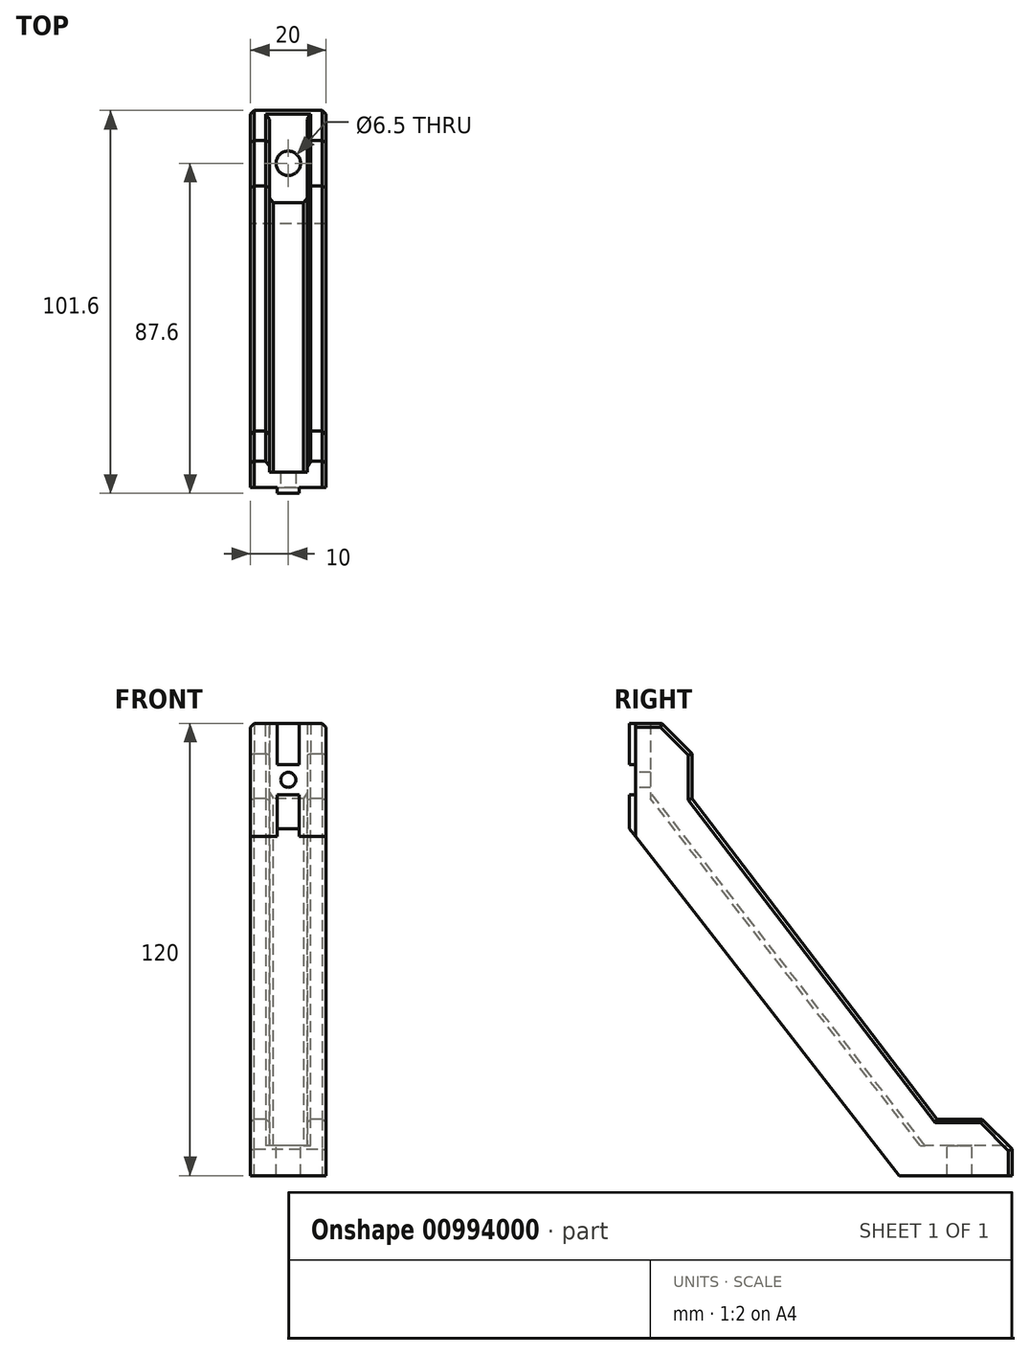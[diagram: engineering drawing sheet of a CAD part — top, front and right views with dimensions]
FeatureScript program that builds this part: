
annotation { "Feature Type Name" : "Feature", "Feature Type Description" : "" }
export const myFeature = defineFeature(function(context is Context, id is Id, definition is map)
    precondition{}
    {
        {
            var Q0;
            Q0=qCreatedBy(makeId("Right.planeOp"),FACE);
            var sketch = newSketch(context, id + "F0", { "sketchPlane" : qUnion([Q0])});
            skLineSegment(sketch, "E0", {"start": v(0, 0) * mm, "end": v(100, 0) * mm, "construction": true});
            skLineSegment(sketch, "E1", {"start": v(0, 0) * mm, "end": v(0, 120) * mm, "construction": true});
            skLineSegment(sketch, "E2", {"start": v(100, 0) * mm, "end": v(70, 0) * mm});
            skLineSegment(sketch, "E3", {"start": v(0, 120) * mm, "end": v(0, 90) * mm});
            skLineSegment(sketch, "E4", {"start": v(100, 0) * mm, "end": v(100, 15) * mm});
            skLineSegment(sketch, "E5", {"start": v(0, 120) * mm, "end": v(15, 120) * mm});
            skLineSegment(sketch, "E6", {"start": v(15, 120) * mm, "end": v(15, 100) * mm});
            skLineSegment(sketch, "E7", {"start": v(15, 100) * mm, "end": v(80, 15) * mm});
            skLineSegment(sketch, "E8", {"start": v(80, 15) * mm, "end": v(100, 15) * mm});
            skLineSegment(sketch, "E9", {"start": v(0, 90) * mm, "end": v(70, 0) * mm});
            skSolve(sketch);
        }
        {
            var Q0;
            Q0 = qSketchRegion(id + "F0", true);
            extrude(context, id + "F1", {"entities" : qUnion([Q0]), "endBound" : BoundingType.SYMMETRIC, "depth" : 20 * mm, "offsetDistance" : 25 * mm});
        }
        {
            var Q0;
            Q0=makeQuery(id+"F1.opExtrude","SWEPT_FACE",FACE,{"disambiguationData":[OSD([sQuery(id+"F0.wireOp",EDGE,"E3")])]});
            var sketch = newSketch(context, id + "F2", { "sketchPlane" : qUnion([Q0])});
            skLineSegment(sketch, "E10", {"start": v(0, 120) * mm, "end": v(0, 90) * mm, "construction": true});
            skLineSegment(sketch, "E11", {"start": v(-2.9, 120) * mm, "end": v(-2.9, 90) * mm});
            skLineSegment(sketch, "E12.MirrorCS", {"start": v(2.9, 120) * mm, "end": v(2.9, 90) * mm});
            skSolve(sketch);
        }
        {
            var Q0;
            {var subQ0=sQuery(id+"F2.wireOp",EDGE,"E11");Q0=makeQuery(id+"F2.imprint","IMPRINT",FACE,{"disambiguationData":[TD([[makeQuery(id+"F2.imprint","IMPRINT",EDGE,{"derivedFrom":subQ0}),1.0]])]});}
            extrude(context, id + "F3", {"entities" : qUnion([Q0]), "operationType" : NewBodyOperationType.ADD, "depth" : 1.6 * mm, "offsetDistance" : 25 * mm});
        }
        {
            var Q0;
            Q0=makeQuery(id+"F3.opExtrude","CAP_FACE",FACE,{"disambiguationData":[OSD([sQuery(id+"F0.wireOp",EDGE,"E3"),sQuery(id+"F0.wireOp",EDGE,"E5"),sQuery(id+"F0.wireOp",EDGE,"E9"),sQuery(id+"F2.wireOp",EDGE,"E11"),sQuery(id+"F2.wireOp",EDGE,"E12.MirrorCS")])],"isStart":false});
            var sketch = newSketch(context, id + "F4", { "sketchPlane" : qUnion([Q0])});
            skLineSegment(sketch, "E13", {"start": v(-2.9, 105) * mm, "end": v(2.9, 105) * mm, "construction": true});
            skLineSegment(sketch, "E14", {"start": v(-2.9, 109) * mm, "end": v(2.9, 109) * mm});
            skLineSegment(sketch, "E15.MirrorCS", {"start": v(-2.9, 101) * mm, "end": v(2.9, 101) * mm});
            skSolve(sketch);
        }
        {
            var Q0;
            {var subQ0=sQuery(id+"F4.wireOp",EDGE,"E14");Q0=makeQuery(id+"F4.imprint","IMPRINT",FACE,{"disambiguationData":[TD([[makeQuery(id+"F4.imprint","IMPRINT",EDGE,{"derivedFrom":subQ0}),-1.0]])]});}
            var Q1;
            {var subQ2=sQuery(id+"F0.wireOp",EDGE,"E3");Q1=makeQuery(id+"F3.boolean.opBoolean","SPLIT",FACE,{"disambiguationData":[TD([makeQuery(id+"F3.opExtrude","SWEPT_FACE",FACE,{"disambiguationData":[OSD([sQuery(id+"F2.wireOp",EDGE,"E11")])]})])],"derivedFrom":makeQuery(id+"F1.opExtrude","SWEPT_FACE",FACE,{"disambiguationData":[OSD([subQ2])]})});}
            extrude(context, id + "F5", {"entities" : qUnion([Q0]), "operationType" : NewBodyOperationType.REMOVE, "endBound" : BoundingType.UP_TO_SURFACE, "oppositeDirection" : true, "depth" : 25 * mm, "endBoundEntityFace" : qUnion([Q1]), "offsetDistance" : 25 * mm});
        }
        {
            var Q0;
            {var subQ0=sQuery(id+"F2.wireOp",EDGE,"E12.MirrorCS");var subQ1=sQuery(id+"F2.wireOp",EDGE,"E11");var subQ6=sQuery(id+"F0.wireOp",EDGE,"E3");var subQ14=makeQuery(id+"F1.opExtrude","SWEPT_FACE",FACE,{"disambiguationData":[OSD([subQ6])]});Q0=makeQuery(id+"F5.boolean.opBoolean","MERGE",FACE,{"derivedFrom":[makeQuery(id+"F3.boolean.opBoolean","SPLIT",FACE,{"disambiguationData":[TD([makeQuery(id+"F3.opExtrude","SWEPT_FACE",FACE,{"disambiguationData":[OSD([subQ1])]})])],"derivedFrom":subQ14}),makeQuery(id+"F3.boolean.opBoolean","SPLIT",FACE,{"disambiguationData":[TD([makeQuery(id+"F3.opExtrude","SWEPT_FACE",FACE,{"disambiguationData":[OSD([subQ0])]})])],"derivedFrom":subQ14})],"fromTools":[makeQuery(id+"F5.opExtrude","CAP_FACE",FACE,{"disambiguationData":[OSD([subQ1,subQ0,sQuery(id+"F4.wireOp",EDGE,"E14"),sQuery(id+"F4.wireOp",EDGE,"E15.MirrorCS")])],"isStart":false})]});}
            var sketch = newSketch(context, id + "F6", { "sketchPlane" : qUnion([Q0])});
            skLineSegment(sketch, "E16", {"start": v(0, 109) * mm, "end": v(0, 101) * mm, "construction": true});
            skCircle(sketch, "E17", {"center": v(0, 105) * mm, "radius": 2 * mm});
            skSolve(sketch);
        }
        {
            var Q0;
            Q0=makeQuery(id+"F6.imprint","IMPRINT",FACE,{"disambiguationData":[TD([[makeQuery(id+"F6.imprint","IMPRINT",EDGE,{"derivedFrom":sQuery(id+"F6.wireOp",EDGE,"E17")}),1.0]])]});
            extrude(context, id + "F7", {"entities" : qUnion([Q0]), "operationType" : NewBodyOperationType.REMOVE, "endBound" : BoundingType.UP_TO_NEXT, "oppositeDirection" : true, "depth" : 25 * mm, "offsetDistance" : 25 * mm});
        }
        {
            var Q0;
            Q0=qCreatedBy(makeId("Right.planeOp"),FACE);
            var sketch = newSketch(context, id + "F8", { "sketchPlane" : qUnion([Q0])});
            skLineSegment(sketch, "E18", {"start": v(0, 0) * mm, "end": v(0, 120) * mm, "construction": true});
            skLineSegment(sketch, "E19", {"start": v(0, 0) * mm, "end": v(100, 0) * mm, "construction": true});
            skLineSegment(sketch, "E20", {"start": v(4, 120) * mm, "end": v(4, 100) * mm});
            skLineSegment(sketch, "E21", {"start": v(4, 100) * mm, "end": v(75.56, 8) * mm});
            skLineSegment(sketch, "E22", {"start": v(100, 8) * mm, "end": v(75.56, 8) * mm});
            skLineSegment(sketch, "E23", {"start": v(100, 0) * mm, "end": v(100, 8) * mm, "construction": true});
            skLineSegment(sketch, "E24", {"start": v(0, 120) * mm, "end": v(4, 120) * mm, "construction": true});
            skLineSegment(sketch, "E25", {"start": v(4, 120) * mm, "end": v(21.82, 120) * mm});
            skLineSegment(sketch, "E26", {"start": v(21.82, 120) * mm, "end": v(100, 19.49) * mm});
            skLineSegment(sketch, "E27", {"start": v(100, 19.49) * mm, "end": v(100, 8) * mm});
            skSolve(sketch);
        }
        {
            var Q0;
            Q0 = qSketchRegion(id + "F8", true);
            extrude(context, id + "F9", {"entities" : qUnion([Q0]), "operationType" : NewBodyOperationType.REMOVE, "endBound" : BoundingType.SYMMETRIC, "depth" : 10 * mm, "offsetDistance" : 25 * mm});
        }
        {
            var Q0;
            Q0=makeQuery(id+"F9.boolean.opBoolean","COPY",FACE,{"derivedFrom":makeQuery(id+"F9.opExtrude","SWEPT_FACE",FACE,{"disambiguationData":[OSD([sQuery(id+"F8.wireOp",EDGE,"E22")])]})});
            var sketch = newSketch(context, id + "F10", { "sketchPlane" : qUnion([Q0])});
            skLineSegment(sketch, "E28", {"start": v(0, 100) * mm, "end": v(0, 75.56) * mm, "construction": true});
            skCircle(sketch, "E29", {"center": v(0, 86) * mm, "radius": 3.25 * mm});
            skSolve(sketch);
        }
        {
            var Q0;
            Q0=makeQuery(id+"F10.imprint","IMPRINT",FACE,{"disambiguationData":[TD([[makeQuery(id+"F10.imprint","IMPRINT",EDGE,{"derivedFrom":sQuery(id+"F10.wireOp",EDGE,"E29")}),1.0]])]});
            extrude(context, id + "F11", {"entities" : qUnion([Q0]), "operationType" : NewBodyOperationType.REMOVE, "endBound" : BoundingType.UP_TO_NEXT, "oppositeDirection" : true, "depth" : 25 * mm, "offsetDistance" : 25 * mm});
        }
        {
            var Q0;
            {var subQ0=sQuery(id+"F2.wireOp",EDGE,"E12.MirrorCS");var subQ2=sQuery(id+"F0.wireOp",EDGE,"E9");Q0=makeQuery(id+"F5.boolean.opBoolean","SPLIT",FACE,{"disambiguationData":[TD([makeQuery(id+"F1.opExtrude","SWEPT_FACE",FACE,{"disambiguationData":[OSD([subQ2])]})])],"derivedFrom":makeQuery(id+"F3.opExtrude","SWEPT_FACE",FACE,{"disambiguationData":[OSD([subQ0])]})});}
            var sketch = newSketch(context, id + "F12", { "sketchPlane" : qUnion([Q0])});
            skLineSegment(sketch, "E30", {"start": v(0, 90) * mm, "end": v(-1.6, 92.06) * mm});
            skSolve(sketch);
        }
        {
            var Q0;
            {var subQ0=sQuery(id+"F12.wireOp",EDGE,"E30");Q0=makeQuery(id+"F12.imprint","IMPRINT",FACE,{"disambiguationData":[TD([[makeQuery(id+"F12.imprint","IMPRINT",EDGE,{"derivedFrom":subQ0}),1.0]])]});}
            extrude(context, id + "F13", {"entities" : qUnion([Q0]), "operationType" : NewBodyOperationType.REMOVE, "endBound" : BoundingType.UP_TO_NEXT, "oppositeDirection" : true, "depth" : 25 * mm, "offsetDistance" : 25 * mm});
        }
        {
            var Q0;
            {var subQ0=sQuery(id+"F0.wireOp",EDGE,"E6");var subQ1=sQuery(id+"F0.wireOp",EDGE,"E5");Q0=makeQuery(id+"F9.boolean.opBoolean","SPLIT",EDGE,{"disambiguationData":[TD([makeQuery(id+"F9.opExtrude","CAP_FACE",FACE,{"disambiguationData":[OSD([sQuery(id+"F8.wireOp",EDGE,"E20"),sQuery(id+"F8.wireOp",EDGE,"E21"),sQuery(id+"F8.wireOp",EDGE,"E22"),sQuery(id+"F8.wireOp",EDGE,"E25"),sQuery(id+"F8.wireOp",EDGE,"E26"),sQuery(id+"F8.wireOp",EDGE,"E27")])],"isStart":false})])],"derivedFrom":makeQuery(id+"F1.opExtrude","SWEPT_EDGE",EDGE,{"disambiguationData":[OSD([subQ1,subQ0])]})});}
            var Q1;
            {var subQ0=sQuery(id+"F0.wireOp",EDGE,"E5");var subQ2=sQuery(id+"F0.wireOp",EDGE,"E6");Q1=makeQuery(id+"F9.boolean.opBoolean","SPLIT",EDGE,{"disambiguationData":[TD([makeQuery(id+"F9.opExtrude","CAP_FACE",FACE,{"disambiguationData":[OSD([sQuery(id+"F8.wireOp",EDGE,"E20"),sQuery(id+"F8.wireOp",EDGE,"E21"),sQuery(id+"F8.wireOp",EDGE,"E22"),sQuery(id+"F8.wireOp",EDGE,"E25"),sQuery(id+"F8.wireOp",EDGE,"E26"),sQuery(id+"F8.wireOp",EDGE,"E27")])],"isStart":true})])],"derivedFrom":makeQuery(id+"F1.opExtrude","SWEPT_EDGE",EDGE,{"disambiguationData":[OSD([subQ0,subQ2])]})});}
            var Q2;
            {var subQ0=sQuery(id+"F0.wireOp",EDGE,"E8");var subQ1=sQuery(id+"F0.wireOp",EDGE,"E4");Q2=makeQuery(id+"F9.boolean.opBoolean","SPLIT",EDGE,{"disambiguationData":[TD([makeQuery(id+"F9.opExtrude","CAP_FACE",FACE,{"disambiguationData":[OSD([sQuery(id+"F8.wireOp",EDGE,"E20"),sQuery(id+"F8.wireOp",EDGE,"E21"),sQuery(id+"F8.wireOp",EDGE,"E22"),sQuery(id+"F8.wireOp",EDGE,"E25"),sQuery(id+"F8.wireOp",EDGE,"E26"),sQuery(id+"F8.wireOp",EDGE,"E27")])],"isStart":false})])],"derivedFrom":makeQuery(id+"F1.opExtrude","SWEPT_EDGE",EDGE,{"disambiguationData":[OSD([subQ1,subQ0])]})});}
            var Q3;
            {var subQ0=sQuery(id+"F0.wireOp",EDGE,"E8");var subQ1=sQuery(id+"F0.wireOp",EDGE,"E4");Q3=makeQuery(id+"F9.boolean.opBoolean","SPLIT",EDGE,{"disambiguationData":[TD([makeQuery(id+"F9.opExtrude","CAP_FACE",FACE,{"disambiguationData":[OSD([sQuery(id+"F8.wireOp",EDGE,"E20"),sQuery(id+"F8.wireOp",EDGE,"E21"),sQuery(id+"F8.wireOp",EDGE,"E22"),sQuery(id+"F8.wireOp",EDGE,"E25"),sQuery(id+"F8.wireOp",EDGE,"E26"),sQuery(id+"F8.wireOp",EDGE,"E27")])],"isStart":true})])],"derivedFrom":makeQuery(id+"F1.opExtrude","SWEPT_EDGE",EDGE,{"disambiguationData":[OSD([subQ1,subQ0])]})});}
            chamfer(context, id + "F14", {"entities" : qUnion([Q0, Q1, Q2, Q3]), "width" : 8 * mm, "tangentPropagation" : true});
        }
        {
            var Q0;
            Q0=makeQuery(id+"F1.opExtrude","CAP_EDGE",EDGE,{"disambiguationData":[OSD([sQuery(id+"F0.wireOp",EDGE,"E7")])],"isStart":false});
            var Q1;
            Q1=makeQuery(id+"F9.boolean.opBoolean","INTERSECT",EDGE,{"derivedFrom":[makeQuery(id+"F1.opExtrude","SWEPT_FACE",FACE,{"disambiguationData":[OSD([sQuery(id+"F0.wireOp",EDGE,"E7")])]}),makeQuery(id+"F9.opExtrude","CAP_FACE",FACE,{"disambiguationData":[OSD([sQuery(id+"F8.wireOp",EDGE,"E20"),sQuery(id+"F8.wireOp",EDGE,"E21"),sQuery(id+"F8.wireOp",EDGE,"E22"),sQuery(id+"F8.wireOp",EDGE,"E25"),sQuery(id+"F8.wireOp",EDGE,"E26"),sQuery(id+"F8.wireOp",EDGE,"E27")])],"isStart":false})]});
            var Q2;
            Q2=makeQuery(id+"F1.opExtrude","CAP_EDGE",EDGE,{"disambiguationData":[OSD([sQuery(id+"F0.wireOp",EDGE,"E6")])],"isStart":false});
            var Q3;
            Q3=makeQuery(id+"F9.boolean.opBoolean","INTERSECT",EDGE,{"derivedFrom":[makeQuery(id+"F1.opExtrude","SWEPT_FACE",FACE,{"disambiguationData":[OSD([sQuery(id+"F0.wireOp",EDGE,"E6")])]}),makeQuery(id+"F9.opExtrude","CAP_FACE",FACE,{"disambiguationData":[OSD([sQuery(id+"F8.wireOp",EDGE,"E20"),sQuery(id+"F8.wireOp",EDGE,"E21"),sQuery(id+"F8.wireOp",EDGE,"E22"),sQuery(id+"F8.wireOp",EDGE,"E25"),sQuery(id+"F8.wireOp",EDGE,"E26"),sQuery(id+"F8.wireOp",EDGE,"E27")])],"isStart":false})]});
            var Q4;
            Q4=makeQuery(id+"F9.boolean.opBoolean","INTERSECT",EDGE,{"derivedFrom":[makeQuery(id+"F1.opExtrude","SWEPT_FACE",FACE,{"disambiguationData":[OSD([sQuery(id+"F0.wireOp",EDGE,"E6")])]}),makeQuery(id+"F9.opExtrude","CAP_FACE",FACE,{"disambiguationData":[OSD([sQuery(id+"F8.wireOp",EDGE,"E20"),sQuery(id+"F8.wireOp",EDGE,"E21"),sQuery(id+"F8.wireOp",EDGE,"E22"),sQuery(id+"F8.wireOp",EDGE,"E25"),sQuery(id+"F8.wireOp",EDGE,"E26"),sQuery(id+"F8.wireOp",EDGE,"E27")])],"isStart":true})]});
            var Q5;
            Q5=makeQuery(id+"F1.opExtrude","CAP_EDGE",EDGE,{"disambiguationData":[OSD([sQuery(id+"F0.wireOp",EDGE,"E6")])],"isStart":true});
            var Q6;
            Q6=makeQuery(id+"F9.boolean.opBoolean","INTERSECT",EDGE,{"derivedFrom":[makeQuery(id+"F1.opExtrude","SWEPT_FACE",FACE,{"disambiguationData":[OSD([sQuery(id+"F0.wireOp",EDGE,"E7")])]}),makeQuery(id+"F9.opExtrude","CAP_FACE",FACE,{"disambiguationData":[OSD([sQuery(id+"F8.wireOp",EDGE,"E20"),sQuery(id+"F8.wireOp",EDGE,"E21"),sQuery(id+"F8.wireOp",EDGE,"E22"),sQuery(id+"F8.wireOp",EDGE,"E25"),sQuery(id+"F8.wireOp",EDGE,"E26"),sQuery(id+"F8.wireOp",EDGE,"E27")])],"isStart":true})]});
            var Q7;
            Q7=makeQuery(id+"F1.opExtrude","CAP_EDGE",EDGE,{"disambiguationData":[OSD([sQuery(id+"F0.wireOp",EDGE,"E7")])],"isStart":true});
            var Q8;
            Q8=makeQuery(id+"F1.opExtrude","CAP_EDGE",EDGE,{"disambiguationData":[OSD([sQuery(id+"F0.wireOp",EDGE,"E8")])],"isStart":false});
            var Q9;
            Q9=makeQuery(id+"F9.boolean.opBoolean","INTERSECT",EDGE,{"derivedFrom":[makeQuery(id+"F1.opExtrude","SWEPT_FACE",FACE,{"disambiguationData":[OSD([sQuery(id+"F0.wireOp",EDGE,"E8")])]}),makeQuery(id+"F9.opExtrude","CAP_FACE",FACE,{"disambiguationData":[OSD([sQuery(id+"F8.wireOp",EDGE,"E20"),sQuery(id+"F8.wireOp",EDGE,"E21"),sQuery(id+"F8.wireOp",EDGE,"E22"),sQuery(id+"F8.wireOp",EDGE,"E25"),sQuery(id+"F8.wireOp",EDGE,"E26"),sQuery(id+"F8.wireOp",EDGE,"E27")])],"isStart":false})]});
            var Q10;
            Q10=makeQuery(id+"F9.boolean.opBoolean","INTERSECT",EDGE,{"derivedFrom":[makeQuery(id+"F1.opExtrude","SWEPT_FACE",FACE,{"disambiguationData":[OSD([sQuery(id+"F0.wireOp",EDGE,"E8")])]}),makeQuery(id+"F9.opExtrude","CAP_FACE",FACE,{"disambiguationData":[OSD([sQuery(id+"F8.wireOp",EDGE,"E20"),sQuery(id+"F8.wireOp",EDGE,"E21"),sQuery(id+"F8.wireOp",EDGE,"E22"),sQuery(id+"F8.wireOp",EDGE,"E25"),sQuery(id+"F8.wireOp",EDGE,"E26"),sQuery(id+"F8.wireOp",EDGE,"E27")])],"isStart":true})]});
            var Q11;
            Q11=makeQuery(id+"F1.opExtrude","CAP_EDGE",EDGE,{"disambiguationData":[OSD([sQuery(id+"F0.wireOp",EDGE,"E8")])],"isStart":true});
            var Q12;
            Q12=makeQuery(id+"F1.opExtrude","CAP_EDGE",EDGE,{"disambiguationData":[OSD([sQuery(id+"F0.wireOp",EDGE,"E4")])],"isStart":true});
            var Q13;
            Q13=makeQuery(id+"F1.opExtrude","CAP_EDGE",EDGE,{"disambiguationData":[OSD([sQuery(id+"F0.wireOp",EDGE,"E4")])],"isStart":false});
            var Q14;
            Q14=makeQuery(id+"F9.boolean.opBoolean","COPY",EDGE,{"derivedFrom":makeQuery(id+"F9.opExtrude","CAP_EDGE",EDGE,{"disambiguationData":[OSD([sQuery(id+"F8.wireOp",EDGE,"E27")])],"isStart":false})});
            var Q15;
            Q15=makeQuery(id+"F9.boolean.opBoolean","COPY",EDGE,{"derivedFrom":makeQuery(id+"F9.opExtrude","SWEPT_EDGE",EDGE,{"disambiguationData":[OSD([sQuery(id+"F8.wireOp",EDGE,"E22"),sQuery(id+"F8.wireOp",EDGE,"E27")])]})});
            var Q16;
            Q16=makeQuery(id+"F9.boolean.opBoolean","COPY",EDGE,{"derivedFrom":makeQuery(id+"F9.opExtrude","CAP_EDGE",EDGE,{"disambiguationData":[OSD([sQuery(id+"F8.wireOp",EDGE,"E27")])],"isStart":true})});
            var Q17;
            Q17=makeQuery(id+"F1.opExtrude","CAP_EDGE",EDGE,{"disambiguationData":[OSD([sQuery(id+"F0.wireOp",EDGE,"E5")])],"isStart":false});
            var Q18;
            Q18=makeQuery(id+"F9.boolean.opBoolean","COPY",EDGE,{"derivedFrom":makeQuery(id+"F9.opExtrude","CAP_EDGE",EDGE,{"disambiguationData":[OSD([sQuery(id+"F8.wireOp",EDGE,"E25")])],"isStart":false})});
            var Q19;
            Q19=makeQuery(id+"F9.boolean.opBoolean","COPY",EDGE,{"derivedFrom":makeQuery(id+"F9.opExtrude","CAP_EDGE",EDGE,{"disambiguationData":[OSD([sQuery(id+"F8.wireOp",EDGE,"E25")])],"isStart":true})});
            var Q20;
            Q20=makeQuery(id+"F1.opExtrude","CAP_EDGE",EDGE,{"disambiguationData":[OSD([sQuery(id+"F0.wireOp",EDGE,"E5")])],"isStart":true});
            var Q21;
            Q21=makeQuery(id+"F9.boolean.opBoolean","COPY",EDGE,{"derivedFrom":makeQuery(id+"F9.opExtrude","SWEPT_EDGE",EDGE,{"disambiguationData":[OSD([sQuery(id+"F8.wireOp",EDGE,"E20"),sQuery(id+"F8.wireOp",EDGE,"E25")])]})});
            var Q22;
            Q22=makeQuery(id+"F9.boolean.opBoolean","COPY",EDGE,{"derivedFrom":makeQuery(id+"F9.opExtrude","CAP_EDGE",EDGE,{"disambiguationData":[OSD([sQuery(id+"F8.wireOp",EDGE,"E21")])],"isStart":false})});
            var Q23;
            Q23=makeQuery(id+"F9.boolean.opBoolean","COPY",EDGE,{"derivedFrom":makeQuery(id+"F9.opExtrude","CAP_EDGE",EDGE,{"disambiguationData":[OSD([sQuery(id+"F8.wireOp",EDGE,"E21")])],"isStart":true})});
            var Q24;
            {var subQ0=sQuery(id+"F0.wireOp",EDGE,"E8");var subQ1=sQuery(id+"F0.wireOp",EDGE,"E4");var subQ2=makeQuery(id+"F1.opExtrude","CAP_FACE",FACE,{"disambiguationData":[OSD([sQuery(id+"F0.wireOp",EDGE,"E2"),sQuery(id+"F0.wireOp",EDGE,"E3"),subQ1,sQuery(id+"F0.wireOp",EDGE,"E5"),sQuery(id+"F0.wireOp",EDGE,"E6"),sQuery(id+"F0.wireOp",EDGE,"E7"),subQ0,sQuery(id+"F0.wireOp",EDGE,"E9")])],"isStart":false});Q24=makeQuery(id+"F14.opChamfer","BLEND_EDGE",EDGE,{"blendedFrom":[makeQuery(id+"F9.boolean.opBoolean","SPLIT",EDGE,{"disambiguationData":[TD([makeQuery(id+"F9.opExtrude","CAP_FACE",FACE,{"disambiguationData":[OSD([sQuery(id+"F8.wireOp",EDGE,"E20"),sQuery(id+"F8.wireOp",EDGE,"E21"),sQuery(id+"F8.wireOp",EDGE,"E22"),sQuery(id+"F8.wireOp",EDGE,"E25"),sQuery(id+"F8.wireOp",EDGE,"E26"),sQuery(id+"F8.wireOp",EDGE,"E27")])],"isStart":false})])],"derivedFrom":makeQuery(id+"F1.opExtrude","SWEPT_EDGE",EDGE,{"disambiguationData":[OSD([subQ1,subQ0])]})}),subQ2],"blendedInto":[subQ2]});}
            var Q25;
            {var subQ0=makeQuery(id+"F9.opExtrude","CAP_FACE",FACE,{"disambiguationData":[OSD([sQuery(id+"F8.wireOp",EDGE,"E20"),sQuery(id+"F8.wireOp",EDGE,"E21"),sQuery(id+"F8.wireOp",EDGE,"E22"),sQuery(id+"F8.wireOp",EDGE,"E25"),sQuery(id+"F8.wireOp",EDGE,"E26"),sQuery(id+"F8.wireOp",EDGE,"E27")])],"isStart":false});var subQ1=sQuery(id+"F0.wireOp",EDGE,"E8");var subQ2=sQuery(id+"F0.wireOp",EDGE,"E4");Q25=makeQuery(id+"F14.opChamfer","BLEND_EDGE",EDGE,{"blendedFrom":[makeQuery(id+"F9.boolean.opBoolean","SPLIT",EDGE,{"disambiguationData":[TD([subQ0])],"derivedFrom":makeQuery(id+"F1.opExtrude","SWEPT_EDGE",EDGE,{"disambiguationData":[OSD([subQ2,subQ1])]})}),makeQuery(id+"F9.boolean.opBoolean","COPY",FACE,{"derivedFrom":subQ0})],"blendedInto":[makeQuery(id+"F9.boolean.opBoolean","COPY",FACE,{"derivedFrom":subQ0})]});}
            var Q26;
            {var subQ0=sQuery(id+"F8.wireOp",EDGE,"E27");var subQ1=sQuery(id+"F8.wireOp",EDGE,"E26");var subQ2=sQuery(id+"F8.wireOp",EDGE,"E25");var subQ3=sQuery(id+"F8.wireOp",EDGE,"E22");var subQ4=sQuery(id+"F8.wireOp",EDGE,"E21");var subQ5=sQuery(id+"F8.wireOp",EDGE,"E20");var subQ6=sQuery(id+"F0.wireOp",EDGE,"E8");var subQ7=sQuery(id+"F0.wireOp",EDGE,"E4");Q26=makeQuery(id+"F14.opChamfer","BLEND_EDGE",EDGE,{"blendedFrom":[makeQuery(id+"F9.boolean.opBoolean","SPLIT",EDGE,{"disambiguationData":[TD([makeQuery(id+"F9.opExtrude","CAP_FACE",FACE,{"disambiguationData":[OSD([subQ5,subQ4,subQ3,subQ2,subQ1,subQ0])],"isStart":false})])],"derivedFrom":makeQuery(id+"F1.opExtrude","SWEPT_EDGE",EDGE,{"disambiguationData":[OSD([subQ7,subQ6])]})}),makeQuery(id+"F9.boolean.opBoolean","COPY",FACE,{"derivedFrom":makeQuery(id+"F9.opExtrude","CAP_FACE",FACE,{"disambiguationData":[OSD([subQ5,subQ4,subQ3,subQ2,subQ1,subQ0])],"isStart":true})})],"blendedInto":[makeQuery(id+"F9.boolean.opBoolean","COPY",FACE,{"derivedFrom":makeQuery(id+"F9.opExtrude","CAP_FACE",FACE,{"disambiguationData":[OSD([subQ5,subQ4,subQ3,subQ2,subQ1,subQ0])],"isStart":true})})]});}
            var Q27;
            {var subQ0=sQuery(id+"F0.wireOp",EDGE,"E9");var subQ1=sQuery(id+"F0.wireOp",EDGE,"E8");var subQ2=sQuery(id+"F0.wireOp",EDGE,"E7");var subQ3=sQuery(id+"F0.wireOp",EDGE,"E6");var subQ4=sQuery(id+"F0.wireOp",EDGE,"E5");var subQ5=sQuery(id+"F0.wireOp",EDGE,"E4");var subQ6=sQuery(id+"F0.wireOp",EDGE,"E3");var subQ7=sQuery(id+"F0.wireOp",EDGE,"E2");Q27=makeQuery(id+"F14.opChamfer","BLEND_EDGE",EDGE,{"blendedFrom":[makeQuery(id+"F9.boolean.opBoolean","SPLIT",EDGE,{"disambiguationData":[TD([makeQuery(id+"F9.opExtrude","CAP_FACE",FACE,{"disambiguationData":[OSD([sQuery(id+"F8.wireOp",EDGE,"E20"),sQuery(id+"F8.wireOp",EDGE,"E21"),sQuery(id+"F8.wireOp",EDGE,"E22"),sQuery(id+"F8.wireOp",EDGE,"E25"),sQuery(id+"F8.wireOp",EDGE,"E26"),sQuery(id+"F8.wireOp",EDGE,"E27")])],"isStart":false})])],"derivedFrom":makeQuery(id+"F1.opExtrude","SWEPT_EDGE",EDGE,{"disambiguationData":[OSD([subQ5,subQ1])]})}),makeQuery(id+"F1.opExtrude","CAP_FACE",FACE,{"disambiguationData":[OSD([subQ7,subQ6,subQ5,subQ4,subQ3,subQ2,subQ1,subQ0])],"isStart":true})],"blendedInto":[makeQuery(id+"F1.opExtrude","CAP_FACE",FACE,{"disambiguationData":[OSD([subQ7,subQ6,subQ5,subQ4,subQ3,subQ2,subQ1,subQ0])],"isStart":true})]});}
            var Q28;
            {var subQ0=sQuery(id+"F0.wireOp",EDGE,"E6");var subQ1=sQuery(id+"F0.wireOp",EDGE,"E5");var subQ2=sQuery(id+"F0.wireOp",EDGE,"E3");var subQ3=makeQuery(id+"F1.opExtrude","CAP_FACE",FACE,{"disambiguationData":[OSD([sQuery(id+"F0.wireOp",EDGE,"E2"),subQ2,sQuery(id+"F0.wireOp",EDGE,"E4"),subQ1,subQ0,sQuery(id+"F0.wireOp",EDGE,"E7"),sQuery(id+"F0.wireOp",EDGE,"E8"),sQuery(id+"F0.wireOp",EDGE,"E9")])],"isStart":false});Q28=makeQuery(id+"F14.opChamfer","BLEND_EDGE",EDGE,{"blendedFrom":[makeQuery(id+"F9.boolean.opBoolean","SPLIT",EDGE,{"disambiguationData":[TD([makeQuery(id+"F9.opExtrude","CAP_FACE",FACE,{"disambiguationData":[OSD([sQuery(id+"F8.wireOp",EDGE,"E20"),sQuery(id+"F8.wireOp",EDGE,"E21"),sQuery(id+"F8.wireOp",EDGE,"E22"),sQuery(id+"F8.wireOp",EDGE,"E25"),sQuery(id+"F8.wireOp",EDGE,"E26"),sQuery(id+"F8.wireOp",EDGE,"E27")])],"isStart":false})])],"derivedFrom":makeQuery(id+"F1.opExtrude","SWEPT_EDGE",EDGE,{"disambiguationData":[OSD([subQ1,subQ0])]})}),subQ3],"blendedInto":[subQ3]});}
            var Q29;
            {var subQ0=makeQuery(id+"F9.opExtrude","CAP_FACE",FACE,{"disambiguationData":[OSD([sQuery(id+"F8.wireOp",EDGE,"E20"),sQuery(id+"F8.wireOp",EDGE,"E21"),sQuery(id+"F8.wireOp",EDGE,"E22"),sQuery(id+"F8.wireOp",EDGE,"E25"),sQuery(id+"F8.wireOp",EDGE,"E26"),sQuery(id+"F8.wireOp",EDGE,"E27")])],"isStart":false});var subQ1=sQuery(id+"F0.wireOp",EDGE,"E6");var subQ2=sQuery(id+"F0.wireOp",EDGE,"E5");Q29=makeQuery(id+"F14.opChamfer","BLEND_EDGE",EDGE,{"blendedFrom":[makeQuery(id+"F9.boolean.opBoolean","SPLIT",EDGE,{"disambiguationData":[TD([subQ0])],"derivedFrom":makeQuery(id+"F1.opExtrude","SWEPT_EDGE",EDGE,{"disambiguationData":[OSD([subQ2,subQ1])]})}),makeQuery(id+"F9.boolean.opBoolean","COPY",FACE,{"derivedFrom":subQ0})],"blendedInto":[makeQuery(id+"F9.boolean.opBoolean","COPY",FACE,{"derivedFrom":subQ0})]});}
            var Q30;
            {var subQ0=makeQuery(id+"F9.opExtrude","CAP_FACE",FACE,{"disambiguationData":[OSD([sQuery(id+"F8.wireOp",EDGE,"E20"),sQuery(id+"F8.wireOp",EDGE,"E21"),sQuery(id+"F8.wireOp",EDGE,"E22"),sQuery(id+"F8.wireOp",EDGE,"E25"),sQuery(id+"F8.wireOp",EDGE,"E26"),sQuery(id+"F8.wireOp",EDGE,"E27")])],"isStart":true});var subQ1=sQuery(id+"F0.wireOp",EDGE,"E5");var subQ3=sQuery(id+"F0.wireOp",EDGE,"E6");Q30=makeQuery(id+"F14.opChamfer","BLEND_EDGE",EDGE,{"blendedFrom":[makeQuery(id+"F9.boolean.opBoolean","SPLIT",EDGE,{"disambiguationData":[TD([subQ0])],"derivedFrom":makeQuery(id+"F1.opExtrude","SWEPT_EDGE",EDGE,{"disambiguationData":[OSD([subQ1,subQ3])]})}),makeQuery(id+"F9.boolean.opBoolean","COPY",FACE,{"derivedFrom":subQ0})],"blendedInto":[makeQuery(id+"F9.boolean.opBoolean","COPY",FACE,{"derivedFrom":subQ0})]});}
            var Q31;
            {var subQ0=sQuery(id+"F0.wireOp",EDGE,"E6");var subQ1=sQuery(id+"F0.wireOp",EDGE,"E5");var subQ2=sQuery(id+"F0.wireOp",EDGE,"E3");var subQ3=makeQuery(id+"F1.opExtrude","CAP_FACE",FACE,{"disambiguationData":[OSD([sQuery(id+"F0.wireOp",EDGE,"E2"),subQ2,sQuery(id+"F0.wireOp",EDGE,"E4"),subQ1,subQ0,sQuery(id+"F0.wireOp",EDGE,"E7"),sQuery(id+"F0.wireOp",EDGE,"E8"),sQuery(id+"F0.wireOp",EDGE,"E9")])],"isStart":true});Q31=makeQuery(id+"F14.opChamfer","BLEND_EDGE",EDGE,{"blendedFrom":[makeQuery(id+"F9.boolean.opBoolean","SPLIT",EDGE,{"disambiguationData":[TD([makeQuery(id+"F9.opExtrude","CAP_FACE",FACE,{"disambiguationData":[OSD([sQuery(id+"F8.wireOp",EDGE,"E20"),sQuery(id+"F8.wireOp",EDGE,"E21"),sQuery(id+"F8.wireOp",EDGE,"E22"),sQuery(id+"F8.wireOp",EDGE,"E25"),sQuery(id+"F8.wireOp",EDGE,"E26"),sQuery(id+"F8.wireOp",EDGE,"E27")])],"isStart":true})])],"derivedFrom":makeQuery(id+"F1.opExtrude","SWEPT_EDGE",EDGE,{"disambiguationData":[OSD([subQ1,subQ0])]})}),subQ3],"blendedInto":[subQ3]});}
            chamfer(context, id + "F15", {"entities" : qUnion([Q0, Q1, Q2, Q3, Q4, Q5, Q6, Q7, Q8, Q9, Q10, Q11, Q12, Q13, Q14, Q15, Q16, Q17, Q18, Q19, Q20, Q21, Q22, Q23, Q24, Q25, Q26, Q27, Q28, Q29, Q30, Q31]), "width" : 1 * mm, "tangentPropagation" : true});
        }
    });
